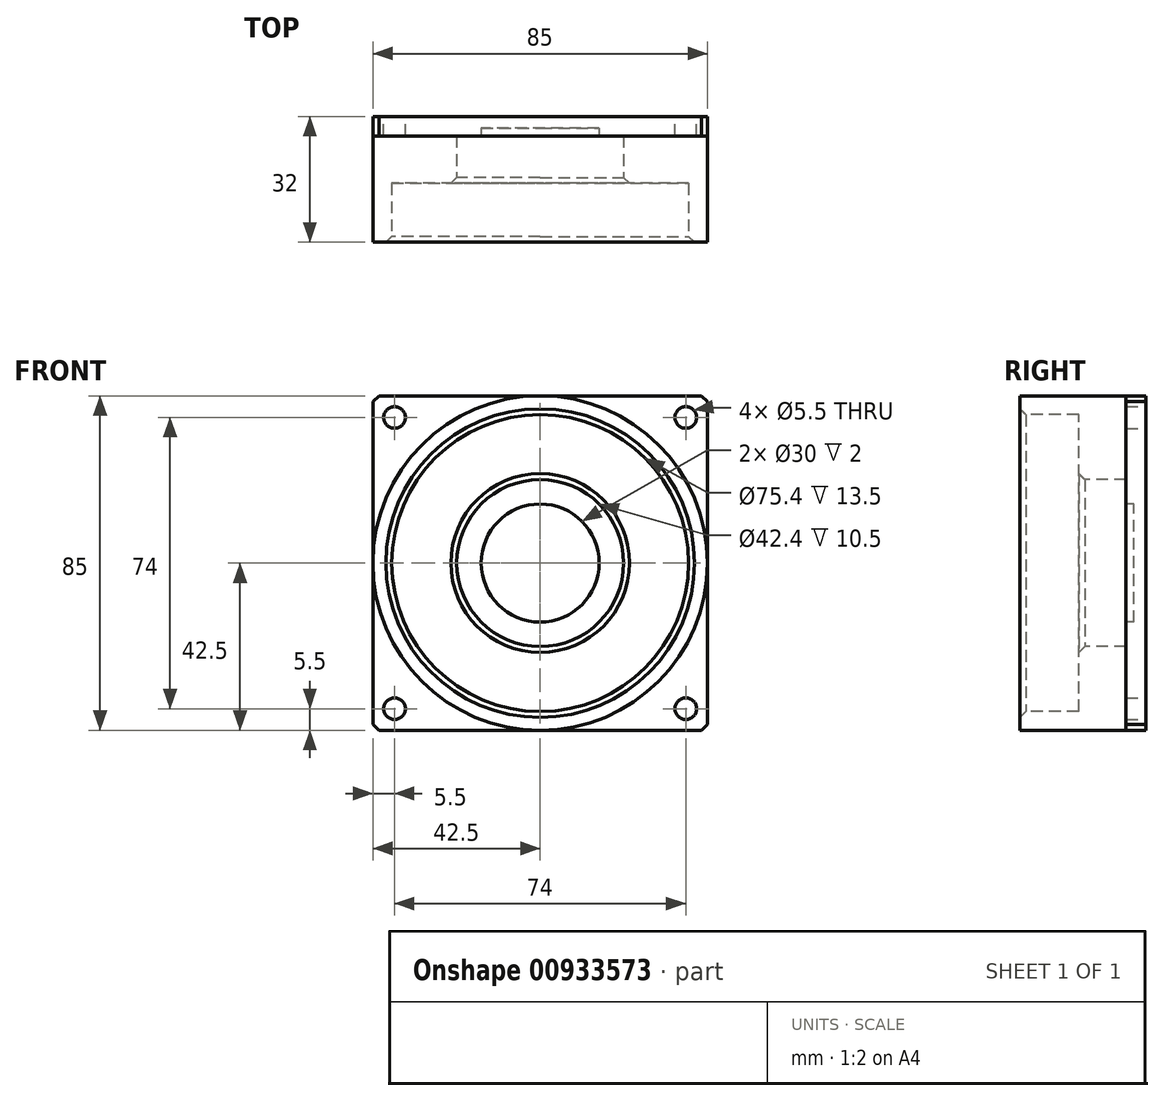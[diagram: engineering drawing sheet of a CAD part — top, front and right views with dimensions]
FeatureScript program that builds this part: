
annotation { "Feature Type Name" : "Feature", "Feature Type Description" : "" }
export const myFeature = defineFeature(function(context is Context, id is Id, definition is map)
    precondition{}
    {
        {
            var Q0;
            Q0=qCreatedBy(makeId("Right.planeOp"),FACE);
            var sketch = newSketch(context, id + "F0", { "sketchPlane" : qUnion([Q0])});
            skLineSegment(sketch, "E0", {"start": v(0, 0) * mm, "end": v(0, 42.5) * mm});
            skLineSegment(sketch, "E1", {"start": v(0, 42.5) * mm, "end": v(-32, 42.5) * mm});
            skLineSegment(sketch, "E2", {"start": v(-32, 42.5) * mm, "end": v(-32, 37.7) * mm});
            skLineSegment(sketch, "E3", {"start": v(-32, 37.7) * mm, "end": v(-17, 37.7) * mm});
            skLineSegment(sketch, "E4", {"start": v(-17, 37.7) * mm, "end": v(-17, 21.2) * mm});
            skLineSegment(sketch, "E5", {"start": v(-17, 21.2) * mm, "end": v(-5, 21.2) * mm});
            skLineSegment(sketch, "E6", {"start": v(-5, 21.2) * mm, "end": v(-5, 0) * mm});
            skLineSegment(sketch, "E7", {"start": v(-5, 0) * mm, "end": v(0, 0) * mm});
            skSolve(sketch);
        }
        {
            var Q0;
            Q0 = qSketchRegion(id + "F0", true);
            var Q1;
            Q1=sQuery(id+"F0.wireOp",EDGE,"E7");
            revolve(context, id + "F1", {"surfaceOperationType" : NewSurfaceOperationType.NEW, "entities" : qUnion([Q0]), "axis" : qUnion([Q1]), "revolveType" : RevolveType.FULL});
        }
        {
            var Q0;
            Q0=qCreatedBy(makeId("Front.planeOp"),FACE);
            var sketch = newSketch(context, id + "F2", { "sketchPlane" : qUnion([Q0])});
            skLineSegment(sketch, "E8.bottom", {"start": v(42.5, 42.5) * mm, "end": v(-42.5, 42.5) * mm});
            skLineSegment(sketch, "E8.top", {"start": v(42.5, -42.5) * mm, "end": v(-42.5, -42.5) * mm});
            skLineSegment(sketch, "E8.left", {"start": v(42.5, 42.5) * mm, "end": v(42.5, -42.5) * mm});
            skLineSegment(sketch, "E8.right", {"start": v(-42.5, 42.5) * mm, "end": v(-42.5, -42.5) * mm});
            skPoint(sketch, "E8.middle", {"position": v(0, 0) * mm});
            skCircle(sketch, "E9", {"center": v(-37, 37) * mm, "radius": 2.75 * mm});
            skCircle(sketch, "E10.MirrorC", {"center": v(37, 37) * mm, "radius": 2.75 * mm});
            skCircle(sketch, "E11.MirrorC", {"center": v(-37, -37) * mm, "radius": 2.75 * mm});
            skCircle(sketch, "E12.MirrorC", {"center": v(37, -37) * mm, "radius": 2.75 * mm});
            skSolve(sketch);
        }
        {
            var Q0;
            Q0 = qSketchRegion(id + "F2", true);
            extrude(context, id + "F3", {"entities" : qUnion([Q0]), "depth" : 5 * mm, "offsetDistance" : 25 * mm});
        }
        {
            var Q0;
            Q0=makeQuery(id+"F1.opRevolve","SWEPT_EDGE",EDGE,{"disambiguationData":[OSD([sQuery(id+"F0.wireOp",EDGE,"E2"),sQuery(id+"F0.wireOp",EDGE,"E3")])]});
            var Q1;
            Q1=makeQuery(id+"F1.opRevolve","SWEPT_EDGE",EDGE,{"disambiguationData":[OSD([sQuery(id+"F0.wireOp",EDGE,"E4"),sQuery(id+"F0.wireOp",EDGE,"E5")])]});
            var Q2;
            Q2=makeQuery(id+"F3.opExtrude","SWEPT_EDGE",EDGE,{"disambiguationData":[OSD([sQuery(id+"F2.wireOp",EDGE,"E8.bottom"),sQuery(id+"F2.wireOp",EDGE,"E8.left")])]});
            var Q3;
            Q3=makeQuery(id+"F3.opExtrude","SWEPT_EDGE",EDGE,{"disambiguationData":[OSD([sQuery(id+"F2.wireOp",EDGE,"E8.bottom"),sQuery(id+"F2.wireOp",EDGE,"E8.right")])]});
            var Q4;
            Q4=makeQuery(id+"F3.opExtrude","SWEPT_EDGE",EDGE,{"disambiguationData":[OSD([sQuery(id+"F2.wireOp",EDGE,"E8.top"),sQuery(id+"F2.wireOp",EDGE,"E8.right")])]});
            var Q5;
            Q5=makeQuery(id+"F3.opExtrude","SWEPT_EDGE",EDGE,{"disambiguationData":[OSD([sQuery(id+"F2.wireOp",EDGE,"E8.top"),sQuery(id+"F2.wireOp",EDGE,"E8.left")])]});
            chamfer(context, id + "F4", {"entities" : qUnion([Q0, Q1, Q2, Q3, Q4, Q5]), "width" : 1.5 * mm, "tangentPropagation" : true});
        }
        {
            var Q0;
            Q0=makeQuery(id+"F1.opRevolve","SWEPT_FACE",FACE,{"disambiguationData":[OSD([sQuery(id+"F0.wireOp",EDGE,"E6")])]});
            var sketch = newSketch(context, id + "F5", { "sketchPlane" : qUnion([Q0])});
            skCircle(sketch, "E13", {"center": v(0, 0) * mm, "radius": 15 * mm});
            skSolve(sketch);
        }
        {
            var Q0;
            Q0 = qSketchRegion(id + "F5", true);
            extrude(context, id + "F6", {"entities" : qUnion([Q0]), "operationType" : NewBodyOperationType.REMOVE, "oppositeDirection" : true, "depth" : 2 * mm, "offsetDistance" : 25 * mm});
        }
    });
